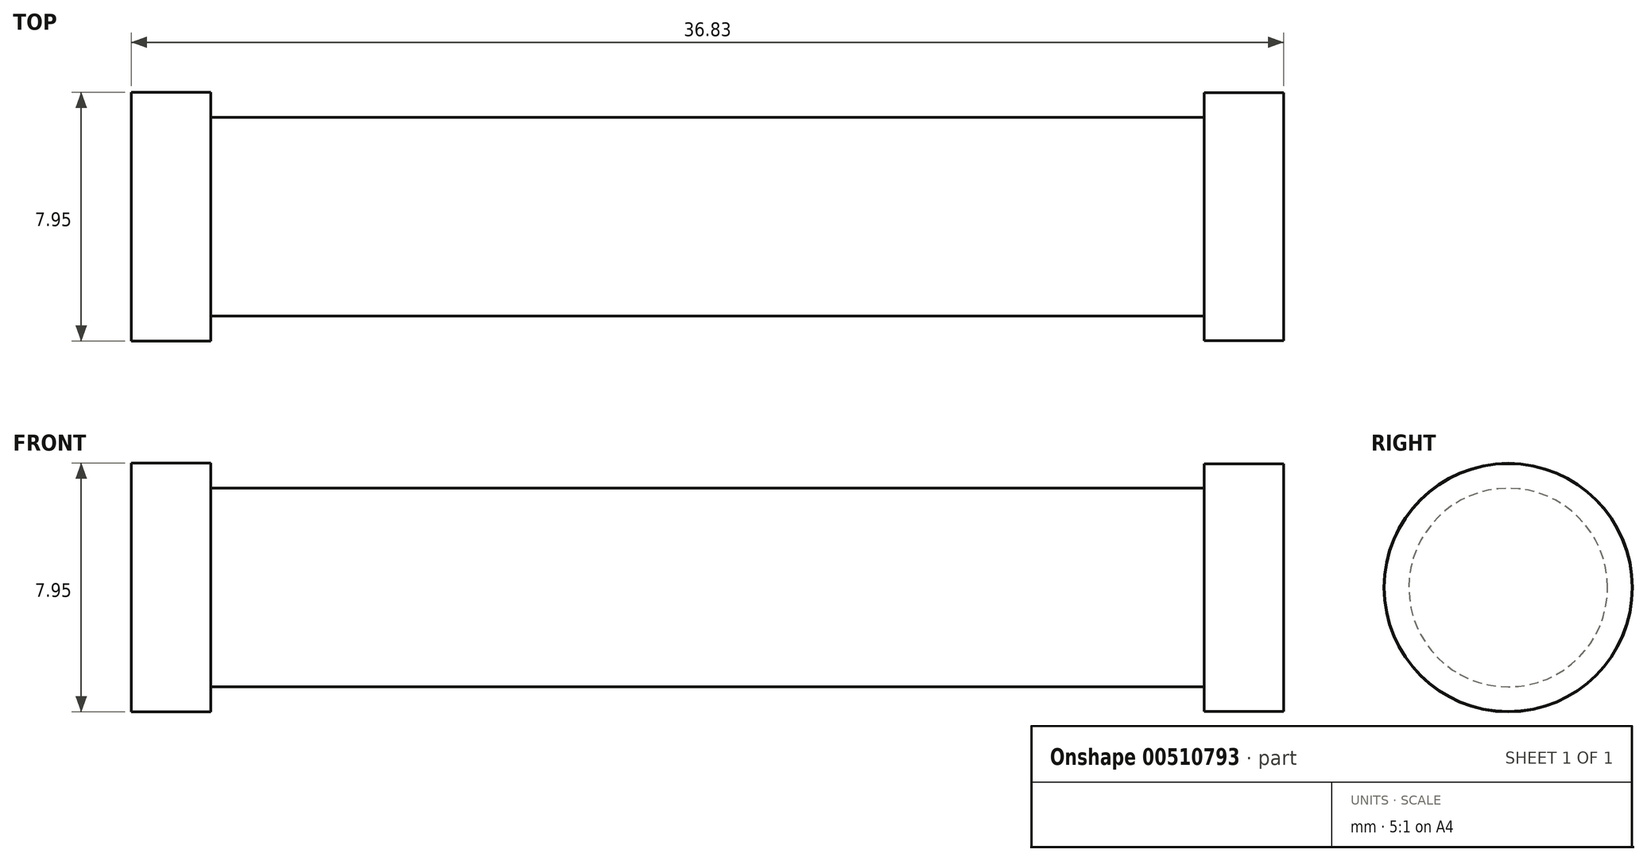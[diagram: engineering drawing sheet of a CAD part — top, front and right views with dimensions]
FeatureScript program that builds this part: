
annotation { "Feature Type Name" : "Feature", "Feature Type Description" : "" }
export const myFeature = defineFeature(function(context is Context, id is Id, definition is map)
    precondition{}
    {
        {
            var Q0;
            Q0=qCreatedBy(makeId("Right.planeOp"),FACE);
            var sketch = newSketch(context, id + "F0", { "sketchPlane" : qUnion([Q0])});
            skCircle(sketch, "E0", {"center": v(-43.17, 38.67) * mm, "radius": 3.18 * mm});
            skSolve(sketch);
        }
        {
            var Q0;
            Q0=qSketchRegion(id+"F0",true);
            extrude(context, id + "F1", {"entities" : qUnion([Q0]), "depth" : 31.75 * mm, "offsetDistance" : 25.4 * mm});
        }
        {
            var Q0;
            Q0=makeQuery(id+"F1.opExtrude","CAP_FACE",FACE,{"disambiguationData":[OSD([sQuery(id+"F0.wireOp",EDGE,"E0")])],"isStart":false});
            var sketch = newSketch(context, id + "F2", { "sketchPlane" : qUnion([Q0])});
            skCircle(sketch, "E1", {"center": v(-43.17, 38.67) * mm, "radius": 3.96 * mm});
            skSolve(sketch);
        }
        {
            var Q0;
            Q0=qSketchRegion(id+"F2",true);
            extrude(context, id + "F3", {"entities" : qUnion([Q0]), "operationType" : NewBodyOperationType.ADD, "depth" : 2.54 * mm, "offsetDistance" : 25.4 * mm});
        }
        {
            var Q0;
            Q0=makeQuery(id+"F1.opExtrude","CAP_FACE",FACE,{"disambiguationData":[OSD([sQuery(id+"F0.wireOp",EDGE,"E0")])],"isStart":true});
            var sketch = newSketch(context, id + "F4", { "sketchPlane" : qUnion([Q0])});
            skCircle(sketch, "E2", {"center": v(43.17, 38.67) * mm, "radius": 3.97 * mm});
            skSolve(sketch);
        }
        {
            var Q0;
            Q0=qSketchRegion(id+"F4",true);
            extrude(context, id + "F5", {"entities" : qUnion([Q0]), "operationType" : NewBodyOperationType.ADD, "depth" : 2.54 * mm, "offsetDistance" : 25.4 * mm});
        }
    });
